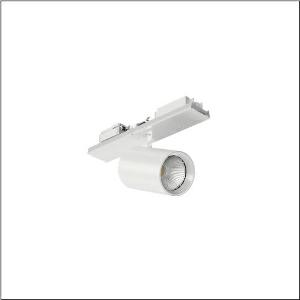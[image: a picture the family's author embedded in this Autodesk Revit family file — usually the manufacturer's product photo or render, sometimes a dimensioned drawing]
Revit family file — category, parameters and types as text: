
# Revit family: licross_spot_31_51sl147a43b
name_source: partatom
category: Lighting Fixtures
units: mm (PartAtom-declared; Revit-internal decimal feet)

## family parameters
Cut with Voids When Loaded = No
Host = Face
Light Source = No
Part Type = Normal
Room Calculation Point = No
Round Connector Dimension = Use Diameter
Shared = No

## types (1)
- --- (1 x LED, 3720 lm, 27.9 W, 4000K)
    Apparent Load = 28 VA
    CIE Flux Codes = 93 97 100 100 100
    Color Rendering = 90
    Color Temperature = 4000K
    Default Elevation = 1800 mm
    Description = Licross Spot 31, directional spotlight, light control with lens, of plastic, LED rated luminous flux: 3.720lm, light colour: 940, with plug, 3-pole, with phase selection, mains connection: 220..240V, AC, 50/60Hz, of aluminium, traffic white (RAL 9016), length: 300mm, diameter: 90mm, protection rating (complete): IP20, insulation class (complete): insulation class I (protective earthing), certification: CE, packaging unit: 1 piece
    Height = 175 mm
    Lamp = 1 x LED
    Lamp Light Flux = 3720 lm
    Lamp Power = 27.9 W
    Lamp count = 1
    Length = 90 mm
    Luminous efficacy = 133 lm/W
    Manufacturer = Siteco
    ModVariant = No
    Model = 51SL147A43B
    Mounting Place = Ceiling
    Mounting Type = Pendant
    Number of Poles = 1
    OnlyDefault = Yes
    Power Factor = 1
    Product Name = Licross Spot 31
    Product group = directional spotlight
    ProductGroupID = 905
    Protection Class = Protection class I
    Protection Degree = IP 20
    RLX_Detail_Level = 1
    RLX_Emergency_Light_Flux = 0 lm
    RLX_Emergency_Type = 0
    RLX_Emergency_Type_DB = No
    RlxData = <blob elided: 14825 chars, md5=4b484df6>
    Socket = socket
    Standby Power = 0 W
    System Light Flux = 3720 lm
    System Power = 28 W
    Type Comments = factory setting: luminous flux: 100 % | (ON | ON | ON) | 700 mA
    Type Image = l_1245720.jpg
    URL = http://relux.com
    VarID = @adj_133133
    Voltage = 0 V
    Weight = 0.00 kg
    Width = 0 mm  [stored 0 ft]

note: [stored X ft] marks values corroborated as IEEE doubles in the binary element streams (Revit-internal decimal feet)

## geometry (parser evidence)
native form markers: Sweep x11
no freeform markers — native parametric forms only
